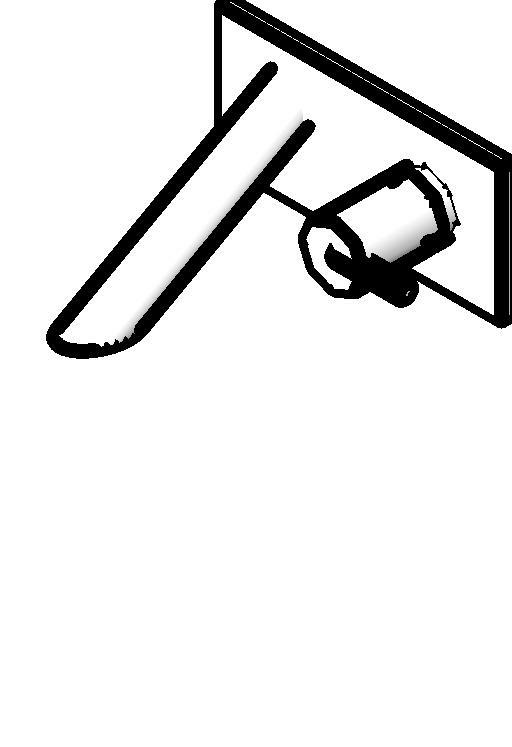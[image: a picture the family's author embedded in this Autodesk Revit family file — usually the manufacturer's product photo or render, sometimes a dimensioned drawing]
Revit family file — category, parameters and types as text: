
# Revit family: Deca_Torneira de parede com fechamento automático para lavatório_Decamatic Eco_1172
name_source: partatom
category: Plumbing Fixtures
units: mm (PartAtom-declared; Revit-internal decimal feet)

## family parameters
Cut with Voids When Loaded = No
Host = Face
Part Type = Normal
Room Calculation Point = No
Round Connector Dimension = Use Radius
Shared = No

## types (1)
- 1172.C_Cromado
    Acompanha o Produto = Acompanha restritor de vazão 8L/Min
    Aprovado por = quattroD
    Atendimento ao Cliente = 0800-0117073
    CWFU = 0
    Categoria = USO PUBLICO
    Composição Anel Vedação = -
    Composição Assento = -
    Composição Básica = Liga de Cobre (bronze e latão),Plásticos de Engenharia,Elastômeros
    Composição Componente = -
    Consumo = -
    Cor Interna = -
    Cor Principal = Cromado
    Cor Secundária = -
    Cores Componente = -
    Criado por = quattroD
    Código Pai = 1172
    Default Elevation = 1100 mm
    Description = Torneira de parede com fechamento automático para lavatório
    Diâmetro Água Fria = 15 mm  [stored 0.0492126 ft]
    Informações Complementares = -
    Itens de Instalação = -
    Linha = Decamatic Eco
    Manufacturer = Deca
    Material = Deca_Cromado
    Model = 1172.C
    Norma = NBR13713
    Peso Líquido (Kg) = 0.995
    Pressão máx. funcionamento = 40 MCA
    Pressão mín. Aquec. Acúmulo = -
    Pressão mín. Aquec. Passagem = -
    Pressão mín. funcionamento = 2 MCA
    Raio Água Fria = 8 mm  [stored 0.0262467 ft]
    Saída de Esgoto = -
    Segmento = Banheiro Competitivo
    Tipo de dispositivo economizador = Sim
    Tipo de mecanismo utilizado = Mecanismo de Fechamento Automático
    Tipo de rosca de entrada = BSP NBR 8133
    Tipo de rosca de saída = -
    URL = www.deca.com.br
    Vazão na Pressão máx. (L/min) = 8
    Vazão na Pressão mín. (L/min) = 5

note: source unit labels omitted for Vazão na Pressão máx. (L/min), Vazão na Pressão mín. (L/min) — the stored unit's dimension contradicts the parameter name (converter mislabeling)

note: [stored X ft] marks values corroborated as IEEE doubles in the binary element streams (Revit-internal decimal feet)

## geometry (parser evidence)
native form markers: Sweep x5
no freeform markers — native parametric forms only
